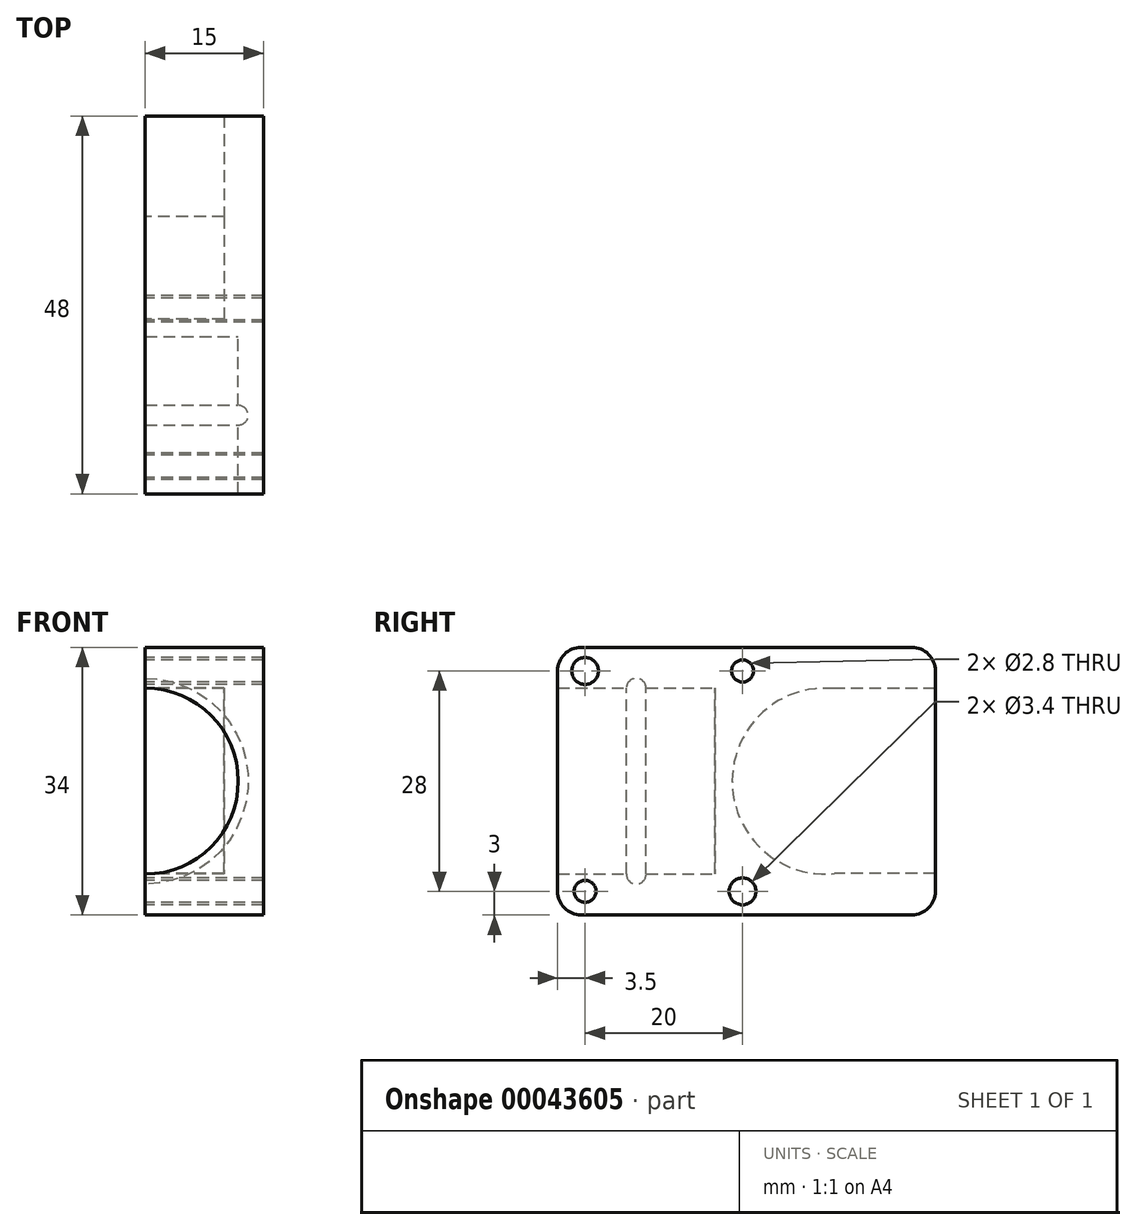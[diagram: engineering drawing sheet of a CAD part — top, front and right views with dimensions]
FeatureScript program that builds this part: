
annotation { "Feature Type Name" : "Feature", "Feature Type Description" : "" }
export const myFeature = defineFeature(function(context is Context, id is Id, definition is map)
    precondition{}
    {
        {
            var Q0;
            Q0=qCreatedBy(makeId("Front.planeOp"),FACE);
            var sketch = newSketch(context, id + "F0", { "sketchPlane" : qUnion([Q0])});
            skLineSegment(sketch, "E0.bottom", {"start": v(0, 17) * mm, "end": v(15, 17) * mm});
            skLineSegment(sketch, "E0.top", {"start": v(0, -17) * mm, "end": v(15, -17) * mm});
            skLineSegment(sketch, "E0.left", {"start": v(0, 17) * mm, "end": v(0, -17) * mm});
            skLineSegment(sketch, "E0.right", {"start": v(15, 17) * mm, "end": v(15, -17) * mm});
            skCircle(sketch, "E1", {"center": v(0, 0) * mm, "radius": 11.8 * mm});
            skPoint(sketch, "E2", {"position": v(0, 14.5) * mm});
            skPoint(sketch, "E3", {"position": v(0, -14.5) * mm});
            skSolve(sketch);
        }
        {
            var Q0;
            {var subQ4=sQuery(id+"F0.wireOp",EDGE,"E0.bottom");Q0=makeQuery(id+"F0.imprint","IMPRINT",FACE,{"disambiguationData":[TD([[makeQuery(id+"F0.imprint","IMPRINT",EDGE,{"derivedFrom":subQ4}),-1.0]])]});}
            extrude(context, id + "F1", {"entities" : qUnion([Q0]), "depth" : 10 * mm, "hasSecondDirection" : true, "secondDirectionOppositeDirection" : true, "secondDirectionDepth" : 10 * mm});
        }
        {
            var Q0;
            {var subQ0=sQuery(id+"F0.wireOp",EDGE,"E0.left");Q0=makeQuery(id+"F1.opExtrude","SWEPT_FACE",FACE,{"disambiguationData":[OSD([subQ0]),TDD([makeQuery(id+"F0.imprint","IMPRINT",EDGE,{"disambiguationData":[TD([[makeQuery(id+"F0.imprint","INTERSECT",VERTEX,{"derivedFrom":[sQuery(id+"F0.wireOp",EDGE,"E0.top"),subQ0]}),1.0]])],"derivedFrom":subQ0})])]});}
            var sketch = newSketch(context, id + "F2", { "sketchPlane" : qUnion([Q0])});
            skPoint(sketch, "E4", {"position": v(-6.5, 14) * mm});
            skPoint(sketch, "E5", {"position": v(6.5, 14) * mm});
            skPoint(sketch, "E6", {"position": v(6.5, -14) * mm});
            skPoint(sketch, "E7", {"position": v(-6.5, -14) * mm});
            skCircle(sketch, "E8", {"center": v(0, -11.8) * mm, "radius": 1.25 * mm});
            skSolve(sketch);
        }
        {
            var Q0;
            {var subQ0=sQuery(id+"F0.wireOp",EDGE,"E0.left");var subQ1=sQuery(id+"F0.wireOp",EDGE,"E1");var subQ2=makeQuery(id+"F1.opExtrude","SWEPT_EDGE",EDGE,{"disambiguationData":[OSD([subQ0,subQ1]),TDD([makeQuery(id+"F0.imprint","INTERSECT",VERTEX,{"disambiguationData":[OD(1.0)],"derivedFrom":[subQ0,subQ1]})])]});var subQ3=sQuery(id+"F2.wireOp",EDGE,"E8");var subQ5=makeQuery(id+"F2.imprint","INTERSECT",VERTEX,{"disambiguationData":[OD(0.0)],"derivedFrom":[subQ2,subQ3]});Q0=makeQuery(id+"F2.imprint","IMPRINT",FACE,{"disambiguationData":[TD([[makeQuery(id+"F2.imprint","IMPRINT",EDGE,{"disambiguationData":[TD([[subQ5,-1.0]])],"derivedFrom":subQ3}),1.0]])]});}
            var Q1;
            Q1=sQuery(id+"F0.wireOp",EDGE,"E1");
            revolve(context, id + "F3", {"operationType" : NewBodyOperationType.REMOVE, "entities" : qUnion([Q0]), "axis" : qUnion([Q1]), "revolveType" : RevolveType.FULL, "oppositeDirection" : true});
        }
        {
            var Q0;
            Q0=makeQuery(id+"F1.opExtrude","CAP_FACE",FACE,{"disambiguationData":[OSD([sQuery(id+"F0.wireOp",EDGE,"E0.bottom"),sQuery(id+"F0.wireOp",EDGE,"E0.top"),sQuery(id+"F0.wireOp",EDGE,"E0.left"),sQuery(id+"F0.wireOp",EDGE,"E0.right"),sQuery(id+"F0.wireOp",EDGE,"E1")])],"isStart":true});
            var sketch = newSketch(context, id + "F4", { "sketchPlane" : qUnion([Q0])});
            skLineSegment(sketch, "E9.bottom", {"start": v(-15, 17) * mm, "end": v(0, 17) * mm});
            skLineSegment(sketch, "E9.top", {"start": v(-15, -17) * mm, "end": v(0, -17) * mm});
            skLineSegment(sketch, "E9.left", {"start": v(-15, 17) * mm, "end": v(-15, -17) * mm});
            skLineSegment(sketch, "E9.right", {"start": v(0, 17) * mm, "end": v(0, -17) * mm});
            skSolve(sketch);
        }
        {
            var Q0;
            {var subQ0=makeQuery(id+"F1.opExtrude","CAP_EDGE",EDGE,{"disambiguationData":[OSD([sQuery(id+"F0.wireOp",EDGE,"E1")])],"isStart":true});Q0=makeQuery(id+"F4.imprint","IMPRINT",FACE,{"disambiguationData":[TD([[makeQuery(id+"F4.imprint","IMPRINT",EDGE,{"derivedFrom":subQ0}),-1.0]])]});}
            var Q1;
            {var subQ3=sQuery(id+"F4.wireOp",EDGE,"E9.bottom");Q1=makeQuery(id+"F4.imprint","IMPRINT",FACE,{"disambiguationData":[TD([[makeQuery(id+"F4.imprint","IMPRINT",EDGE,{"derivedFrom":subQ3}),1.0]])]});}
            extrude(context, id + "F5", {"entities" : qUnion([Q0, Q1]), "depth" : 28 * mm});
        }
        {
            var Q0;
            Q0=makeQuery(id+"F1.opExtrude","SWEPT_BODY",BODY,{"disambiguationData":[OSD([sQuery(id+"F0.wireOp",EDGE,"E0.bottom"),sQuery(id+"F0.wireOp",EDGE,"E0.top"),sQuery(id+"F0.wireOp",EDGE,"E0.left"),sQuery(id+"F0.wireOp",EDGE,"E0.right"),sQuery(id+"F0.wireOp",EDGE,"E1")])]});
            var Q1;
            Q1=makeQuery(id+"F5.opExtrude","SWEPT_BODY",BODY,{"disambiguationData":[OSD([sQuery(id+"F4.wireOp",EDGE,"E9.bottom"),sQuery(id+"F4.wireOp",EDGE,"E9.top"),sQuery(id+"F4.wireOp",EDGE,"E9.left"),sQuery(id+"F4.wireOp",EDGE,"E9.right")])]});
            booleanBodies(context, id + "F6", {"operationType" : BooleanOperationType.UNION, "tools" : qUnion([Q0, Q1])});
        }
        {
            var Q0;
            {var subQ0=sQuery(id+"F0.wireOp",EDGE,"E0.left");Q0=makeQuery(id+"F6.opBoolean","MERGE",FACE,{"derivedFrom":[makeQuery(id+"F1.opExtrude","SWEPT_FACE",FACE,{"disambiguationData":[OSD([subQ0]),TDD([makeQuery(id+"F0.imprint","IMPRINT",EDGE,{"disambiguationData":[TD([[makeQuery(id+"F0.imprint","INTERSECT",VERTEX,{"derivedFrom":[sQuery(id+"F0.wireOp",EDGE,"E0.bottom"),subQ0]}),-1.0]])],"derivedFrom":subQ0})])]}),makeQuery(id+"F1.opExtrude","SWEPT_FACE",FACE,{"disambiguationData":[OSD([subQ0]),TDD([makeQuery(id+"F0.imprint","IMPRINT",EDGE,{"disambiguationData":[TD([[makeQuery(id+"F0.imprint","INTERSECT",VERTEX,{"derivedFrom":[sQuery(id+"F0.wireOp",EDGE,"E0.top"),subQ0]}),1.0]])],"derivedFrom":subQ0})])]}),makeQuery(id+"F5.opExtrude","SWEPT_FACE",FACE,{"disambiguationData":[OSD([sQuery(id+"F4.wireOp",EDGE,"E9.right")])]})]});}
            var sketch = newSketch(context, id + "F7", { "sketchPlane" : qUnion([Q0])});
            skPoint(sketch, "E10", {"position": v(-24, 0) * mm});
            skPoint(sketch, "E11", {"position": v(-34.5, 14) * mm});
            skPoint(sketch, "E12", {"position": v(-13.5, 14) * mm});
            skPoint(sketch, "E13", {"position": v(-13.5, -14) * mm});
            skPoint(sketch, "E14", {"position": v(-34.5, -14) * mm});
            skLineSegment(sketch, "E15.bottom", {"start": v(-38, -11.75) * mm, "end": v(-24, -11.75) * mm});
            skLineSegment(sketch, "E15.top", {"start": v(-38, 11.75) * mm, "end": v(-24, 11.75) * mm});
            skLineSegment(sketch, "E15.left", {"start": v(-38, -11.75) * mm, "end": v(-38, 11.75) * mm});
            skLineSegment(sketch, "E15.right", {"start": v(-24, -11.75) * mm, "end": v(-24, 11.75) * mm});
            skCircle(sketch, "E16", {"center": v(-24, 0) * mm, "radius": 11.8 * mm});
            skSolve(sketch);
        }
        {
            var Q0;
            Q0=sQuery(id+"F7.wireOp",VERTEX,"E12");
            var Q1;
            Q1=sQuery(id+"F2.wireOp",VERTEX,"E6");
            var Q2;
            Q2=makeQuery(id+"F1.opExtrude","SWEPT_BODY",BODY,{"disambiguationData":[OSD([sQuery(id+"F0.wireOp",EDGE,"E0.bottom"),sQuery(id+"F0.wireOp",EDGE,"E0.top"),sQuery(id+"F0.wireOp",EDGE,"E0.left"),sQuery(id+"F0.wireOp",EDGE,"E0.right"),sQuery(id+"F0.wireOp",EDGE,"E1")])]});
            hole(context, id + "F8", {"style" : HoleStyle.SIMPLE, "holeDiameter" : 2.8 * mm, "endStyle" : HoleEndStyle.THROUGH, "locations" : qUnion([Q0, Q1]), "scope" : qUnion([Q2])});
        }
        {
            var Q0;
            Q0=sQuery(id+"F7.wireOp",VERTEX,"E13");
            var Q1;
            Q1=sQuery(id+"F2.wireOp",VERTEX,"E5");
            var Q2;
            Q2=makeQuery(id+"F1.opExtrude","SWEPT_BODY",BODY,{"disambiguationData":[OSD([sQuery(id+"F0.wireOp",EDGE,"E0.bottom"),sQuery(id+"F0.wireOp",EDGE,"E0.top"),sQuery(id+"F0.wireOp",EDGE,"E0.left"),sQuery(id+"F0.wireOp",EDGE,"E0.right"),sQuery(id+"F0.wireOp",EDGE,"E1")])]});
            hole(context, id + "F9", {"style" : HoleStyle.SIMPLE, "holeDiameter" : 3.4 * mm, "endStyle" : HoleEndStyle.THROUGH, "locations" : qUnion([Q0, Q1]), "scope" : qUnion([Q2])});
        }
        {
            var Q0;
            Q0=makeQuery(id+"F7.imprint","IMPRINT",FACE,{"disambiguationData":[TD([[makeQuery(id+"F7.imprint","IMPRINT",EDGE,{"derivedFrom":sQuery(id+"F7.wireOp",EDGE,"E15.bottom")}),1.0]])]});
            extrude(context, id + "F10", {"entities" : qUnion([Q0]), "operationType" : NewBodyOperationType.REMOVE, "oppositeDirection" : true, "depth" : 10 * mm});
        }
        {
            var Q0;
            Q0=makeQuery(id+"F1.opExtrude","CAP_EDGE",EDGE,{"disambiguationData":[OSD([sQuery(id+"F0.wireOp",EDGE,"E0.top")])],"isStart":false});
            var Q1;
            Q1=makeQuery(id+"F1.opExtrude","CAP_EDGE",EDGE,{"disambiguationData":[OSD([sQuery(id+"F0.wireOp",EDGE,"E0.bottom")])],"isStart":false});
            var Q2;
            Q2=makeQuery(id+"F5.opExtrude","CAP_EDGE",EDGE,{"disambiguationData":[OSD([sQuery(id+"F4.wireOp",EDGE,"E9.top")])],"isStart":false});
            var Q3;
            Q3=makeQuery(id+"F5.opExtrude","CAP_EDGE",EDGE,{"disambiguationData":[OSD([sQuery(id+"F4.wireOp",EDGE,"E9.bottom")])],"isStart":false});
            var Q4;
            Q4=makeQuery(id+"F10.boolean.opBoolean","COPY",EDGE,{"derivedFrom":makeQuery(id+"F10.opExtrude","SWEPT_EDGE",EDGE,{"disambiguationData":[OSD([sQuery(id+"F4.wireOp",EDGE,"E9.right"),sQuery(id+"F7.wireOp",EDGE,"E15.bottom"),sQuery(id+"F7.wireOp",EDGE,"E15.left")])]})});
            var Q5;
            Q5=makeQuery(id+"F10.boolean.opBoolean","COPY",EDGE,{"derivedFrom":makeQuery(id+"F10.opExtrude","SWEPT_EDGE",EDGE,{"disambiguationData":[OSD([sQuery(id+"F4.wireOp",EDGE,"E9.right"),sQuery(id+"F7.wireOp",EDGE,"E15.top"),sQuery(id+"F7.wireOp",EDGE,"E15.left")])]})});
            fillet(context, id + "F11", {"entities" : qUnion([Q0, Q1, Q2, Q3, Q4, Q5]), "radius" : 3 * mm, "tangentPropagation" : true, "allowEdgeOverflow" : false});
        }
        {
            var Q0;
            {var subQ5=sQuery(id+"F7.wireOp",EDGE,"E15.right");Q0=makeQuery(id+"F7.imprint","IMPRINT",FACE,{"disambiguationData":[TD([[makeQuery(id+"F7.imprint","IMPRINT",EDGE,{"derivedFrom":subQ5}),-1.0]])]});}
            extrude(context, id + "F12", {"entities" : qUnion([Q0]), "operationType" : NewBodyOperationType.REMOVE, "oppositeDirection" : true, "depth" : 10 * mm});
        }
    });
